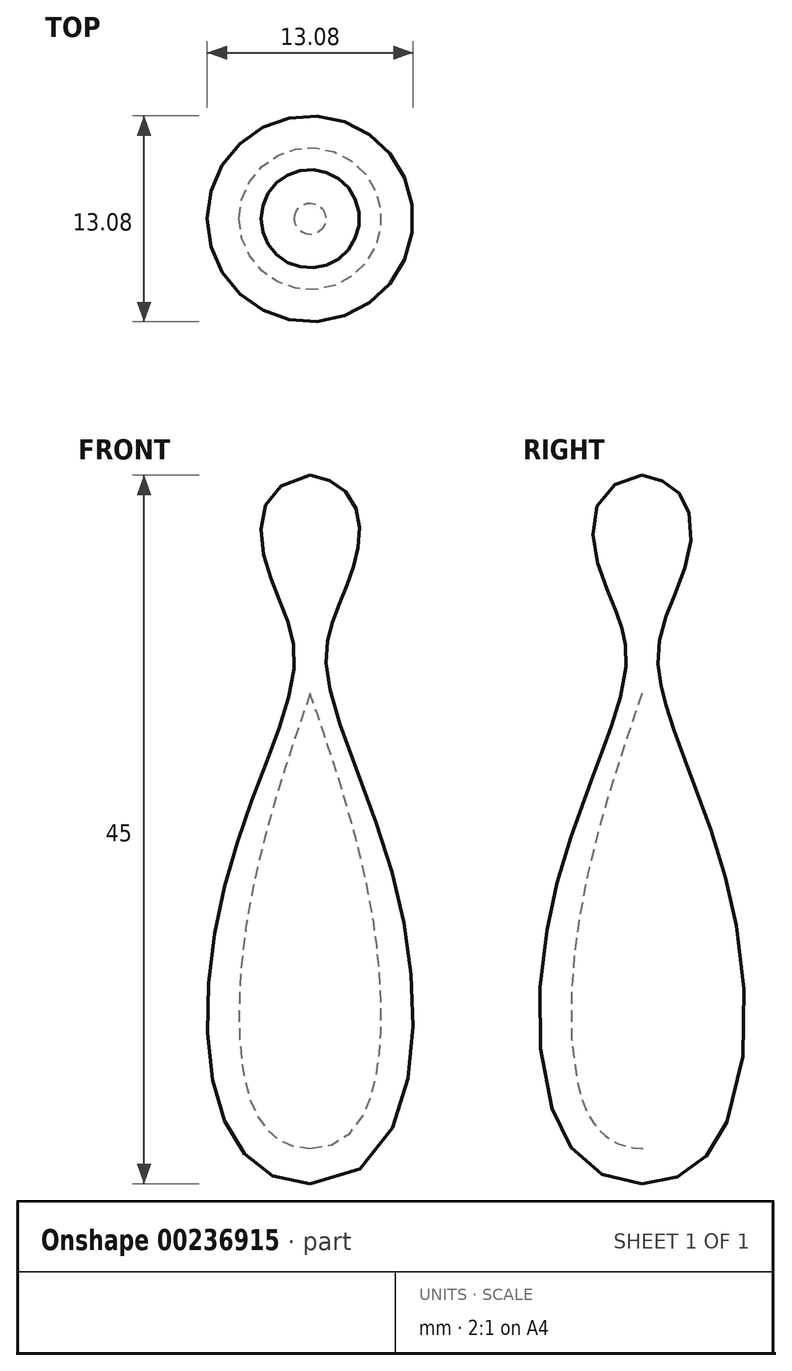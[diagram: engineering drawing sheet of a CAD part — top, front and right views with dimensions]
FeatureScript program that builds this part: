
annotation { "Feature Type Name" : "Feature", "Feature Type Description" : "" }
export const myFeature = defineFeature(function(context is Context, id is Id, definition is map)
    precondition{}
    {
        {
            var Q0;
            Q0=qCreatedBy(makeId("Front.planeOp"),FACE);
            var sketch = newSketch(context, id + "F0", { "sketchPlane" : qUnion([Q0])});
            skLineSegment(sketch, "E0", {"start": v(0, 40.51) * mm, "end": v(0, 19.83) * mm, "construction": true});
            skFitSpline(sketch, "E1", {"points": [v(0, -11.3) * mm, v(-6, 5.1) * mm, v(-1, 21.98) * mm, v(-2.85, 28.27) * mm, v(0, 33.7) * mm], "startDerivative": vector(-62.25, 0.3) * mm, "endDerivative": vector(54.25, 7.92) * mm});
            skLineSegment(sketch, "E2", {"start": v(0, 33.7) * mm, "end": v(0, 19.83) * mm});
            skFitSpline(sketch, "E3", {"points": [v(0, 19.83) * mm, v(-4.5, 0) * mm, v(0, -9.04) * mm], "startDerivative": vector(-13.13, -37.3) * mm, "endDerivative": vector(27.73, 0.05) * mm});
            skLineSegment(sketch, "E4.trimOffspring", {"start": v(0, -9.04) * mm, "end": v(0, -30.87) * mm, "construction": true});
            skLineSegment(sketch, "E5.trimOffspring", {"start": v(0, -9.04) * mm, "end": v(0, -11.3) * mm});
            skSolve(sketch);
        }
        {
            var Q0;
            Q0 = qSketchRegion(id + "F0", true);
            var Q1;
            Q1=sQuery(id+"F0.wireOp",EDGE,"E0");
            revolve(context, id + "F1", {"entities" : qUnion([Q0]), "axis" : qUnion([Q1]), "revolveType" : RevolveType.FULL});
        }
    });
